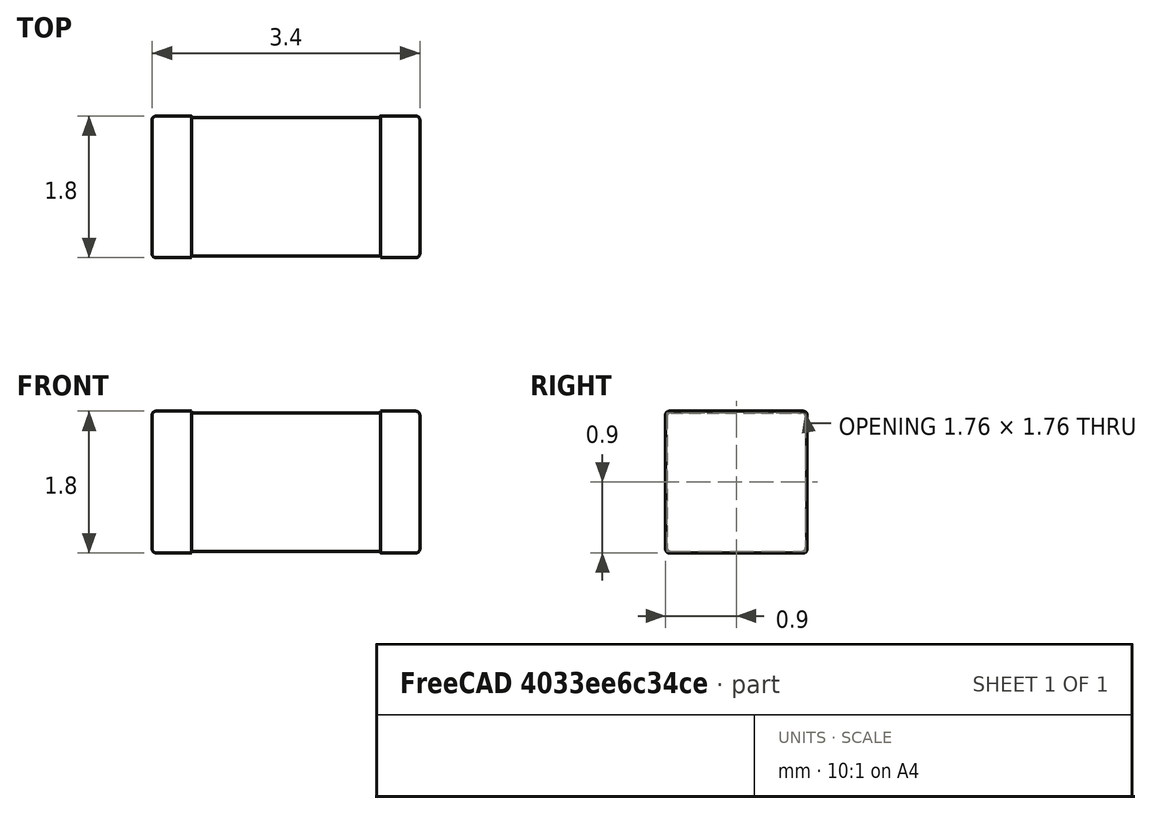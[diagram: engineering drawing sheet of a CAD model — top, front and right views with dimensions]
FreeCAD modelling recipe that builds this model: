
FCSTD DOCUMENT
Label: CAP_CHIP_3216X160
Comment: Kemet C1206... / H1.6+-0.2
objects: Part::Box×3, Part::Fillet×3, Part::MultiFuse×1
note: 7 computed .brp shape members not serialized (recipe doc carries the construction recipe); baked Part::Feature solids carry a one-line shape summary decoded from their .brp

FEATURE [Part::Box] chip
  Height = 1.76
  Length = 3.36
  Placement = pos=(-1.68,-0.88,0.02) rot=(0,0,1;0rad)
  Width = 1.76
FEATURE [Part::Fillet] chip_f
  Base = -> chip
  Edges = 4 edges r=0.05: [Edge9,Edge10,Edge11,Edge12]
FEATURE [Part::Box] plating_left
  Height = 1.8
  Length = 0.5
  Placement = pos=(-1.7,-0.9,0) rot=(0,0,1;0rad)
  Width = 1.8
FEATURE [Part::Fillet] plating_left_f
  Base = -> plating_left
  Edges = 8 edges r=0.05: [Edge1,Edge2,Edge3,Edge4,Edge9,Edge10,Edge11,Edge12]
FEATURE [Part::Box] plating_right
  Height = 1.8
  Length = 0.5
  Placement = pos=(1.2,-0.9,0) rot=(0,0,1;0rad)
  Width = 1.8
FEATURE [Part::Fillet] plating_right_f
  Base = -> plating_right
  Edges = 8 edges r=0.05: [Edge5,Edge6,Edge7,Edge8,Edge9,Edge10,Edge11,Edge12]
FEATURE [Part::MultiFuse] capacitor
  Shapes = -> [chip_f,plating_left_f,plating_right_f]
